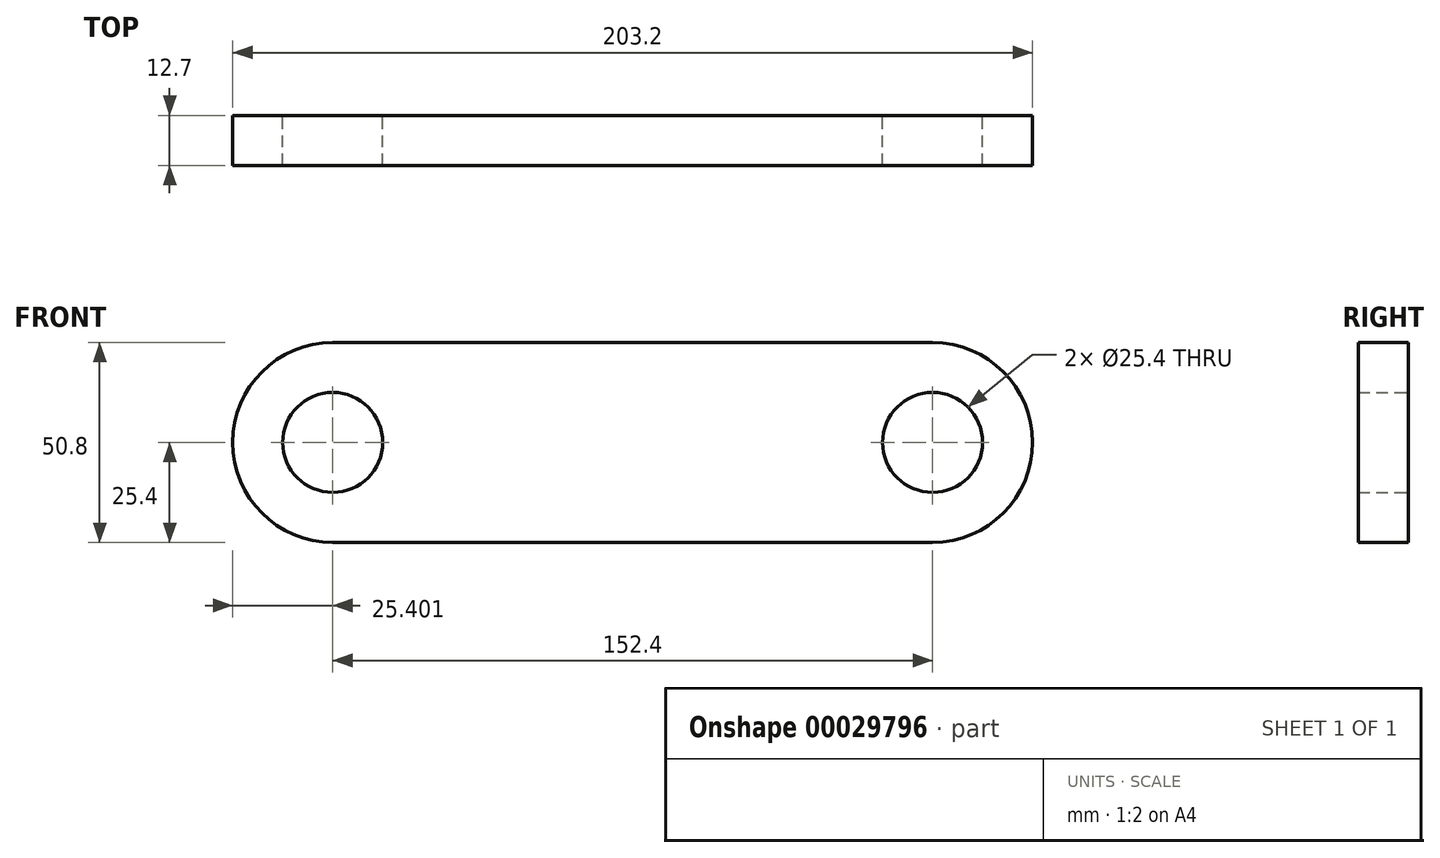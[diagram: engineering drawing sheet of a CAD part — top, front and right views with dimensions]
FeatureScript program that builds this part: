
annotation { "Feature Type Name" : "Feature", "Feature Type Description" : "" }
export const myFeature = defineFeature(function(context is Context, id is Id, definition is map)
    precondition{}
    {
        {
            var Q0;
            Q0=qCreatedBy(makeId("Front.planeOp"),FACE);
            var sketch = newSketch(context, id + "F0", { "sketchPlane" : qUnion([Q0])});
            skLineSegment(sketch, "E0.rect.bottom", {"start": v(70.92, -25.76) * mm, "end": v(-81.48, -25.76) * mm});
            skLineSegment(sketch, "E0.rect.top", {"start": v(70.92, 25.04) * mm, "end": v(-81.48, 25.04) * mm});
            skLineSegment(sketch, "E0.rect.left", {"start": v(70.92, -13.06) * mm, "end": v(70.92, -13.06) * mm});
            skLineSegment(sketch, "E0.rect.right", {"start": v(-81.48, -25.76) * mm, "end": v(-81.48, -25.76) * mm});
            skPoint(sketch, "E0.rect.middle", {"position": v(-5.28, -0.36) * mm});
            skLineSegment(sketch, "E1.trimOffspring", {"start": v(70.92, 12.34) * mm, "end": v(70.92, 12.34) * mm});
            skPoint(sketch, "E2.center.orphan", {"position": v(70.92, -0.36) * mm});
            skArc(sketch, "E3", {"start": v(70.92, -25.76) * mm, "mid": v(96.32, -0.36) * mm, "end": v(70.92, 25.04) * mm});
            skCircle(sketch, "E4", {"center": v(70.92, -0.36) * mm, "radius": 12.7 * mm});
            skLineSegment(sketch, "E5", {"start": v(58.22, -0.06) * mm, "end": v(70.92, -0.36) * mm});
            skArc(sketch, "E6", {"start": v(-81.48, 25.04) * mm, "mid": v(-106.88, -0.36) * mm, "end": v(-81.48, -25.76) * mm});
            skLineSegment(sketch, "E7.trimOffspring", {"start": v(-81.48, 25.04) * mm, "end": v(-81.48, 25.04) * mm});
            skCircle(sketch, "E8", {"center": v(-81.48, -0.36) * mm, "radius": 12.7 * mm});
            skLineSegment(sketch, "E9", {"start": v(-81.48, -0.36) * mm, "end": v(-73.36, 9.4) * mm});
            skSolve(sketch);
        }
        {
            var Q0;
            Q0=makeQuery(id+"F0.imprint","IMPRINT",FACE,{"disambiguationData":[TD([[makeQuery(id+"F0.imprint","IMPRINT",EDGE,{"derivedFrom":sQuery(id+"F0.wireOp",EDGE,"E0.rect.bottom")}),-1.0]])]});
            extrude(context, id + "F1", {"entities" : qUnion([Q0]), "depth" : 12.7 * mm});
        }
    });
